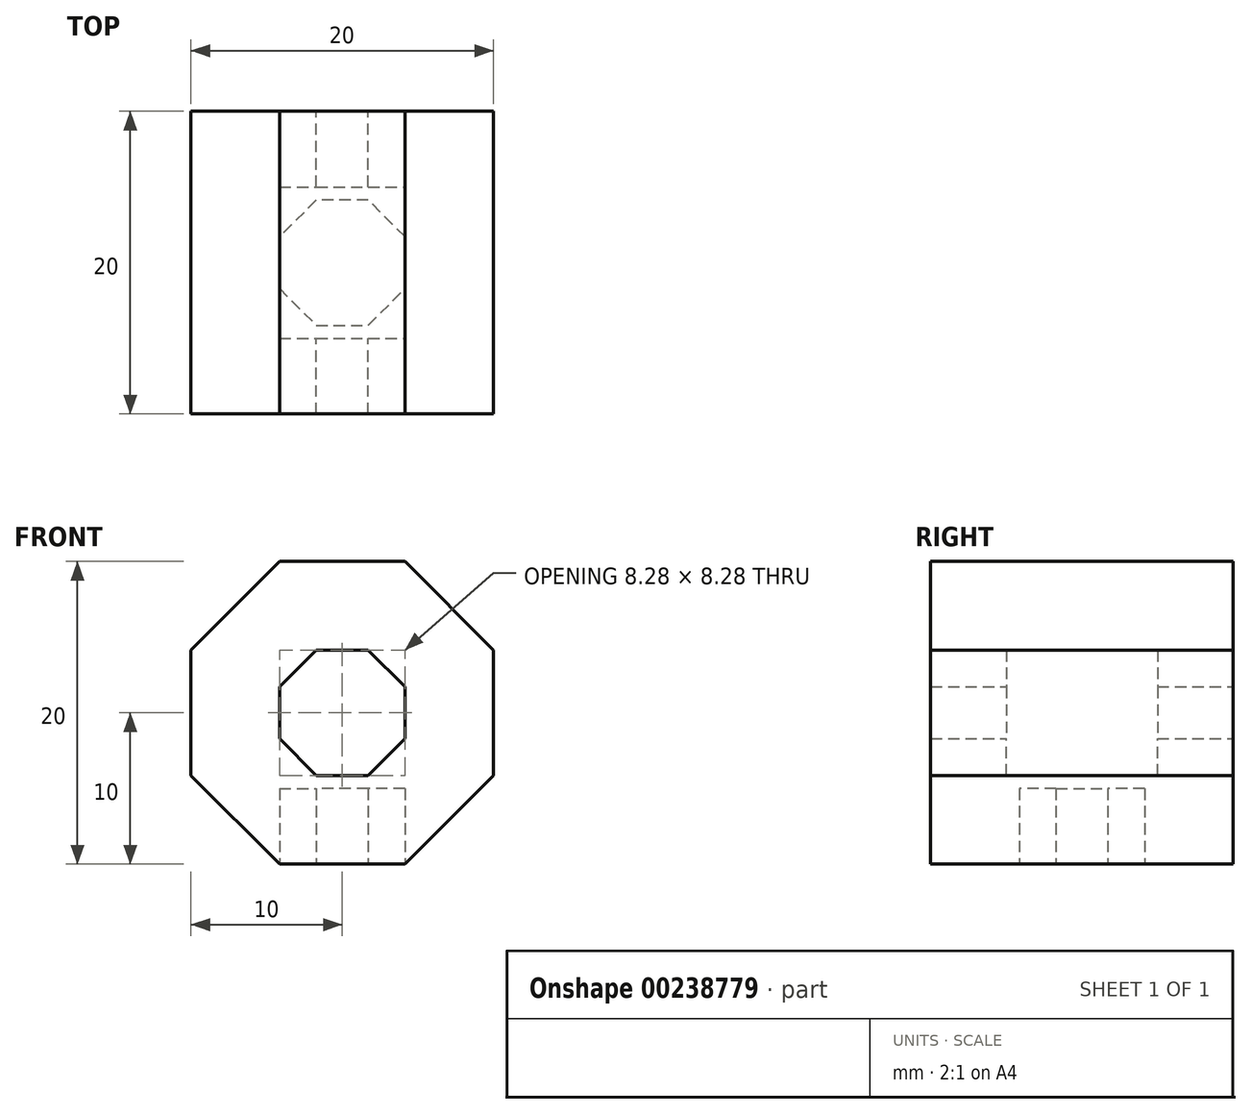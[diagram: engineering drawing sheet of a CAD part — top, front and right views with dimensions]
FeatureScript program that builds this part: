
annotation { "Feature Type Name" : "Feature", "Feature Type Description" : "" }
export const myFeature = defineFeature(function(context is Context, id is Id, definition is map)
    precondition{}
    {
        {
            var Q0;
            Q0=qCreatedBy(makeId("Front.planeOp"),FACE);
            var sketch = newSketch(context, id + "F0", { "sketchPlane" : qUnion([Q0])});
            skLineSegment(sketch, "E0.0", {"start": v(10, -4.14) * mm, "end": v(4.14, -10) * mm});
            skLineSegment(sketch, "E0.1", {"start": v(4.14, -10) * mm, "end": v(-4.14, -10) * mm});
            skLineSegment(sketch, "E0.2", {"start": v(-4.14, -10) * mm, "end": v(-10, -4.14) * mm});
            skLineSegment(sketch, "E0.3", {"start": v(-10, -4.14) * mm, "end": v(-10, 4.14) * mm});
            skLineSegment(sketch, "E0.4", {"start": v(-10, 4.14) * mm, "end": v(-4.14, 10) * mm});
            skLineSegment(sketch, "E0.5", {"start": v(-4.14, 10) * mm, "end": v(4.14, 10) * mm});
            skLineSegment(sketch, "E0.6", {"start": v(4.14, 10) * mm, "end": v(10, 4.14) * mm});
            skLineSegment(sketch, "E0.7", {"start": v(10, 4.14) * mm, "end": v(10, -4.14) * mm});
            skPoint(sketch, "E0.0.midPoint", {"position": v(7.07, -7.07) * mm});
            skLineSegment(sketch, "E1", {"start": v(-1.72, -4.14) * mm, "end": v(1.72, -4.14) * mm});
            skLineSegment(sketch, "E2.0", {"start": v(1.72, 4.14) * mm, "end": v(4.14, 1.72) * mm});
            skLineSegment(sketch, "E2.1", {"start": v(4.14, 1.72) * mm, "end": v(4.14, -1.72) * mm});
            skLineSegment(sketch, "E2.2", {"start": v(4.14, -1.72) * mm, "end": v(1.72, -4.14) * mm});
            skLineSegment(sketch, "E2.3", {"start": v(1.72, -4.14) * mm, "end": v(-1.72, -4.14) * mm});
            skLineSegment(sketch, "E2.4", {"start": v(-1.72, -4.14) * mm, "end": v(-4.14, -1.72) * mm});
            skLineSegment(sketch, "E2.5", {"start": v(-4.14, -1.72) * mm, "end": v(-4.14, 1.72) * mm});
            skLineSegment(sketch, "E2.6", {"start": v(-4.14, 1.72) * mm, "end": v(-1.72, 4.14) * mm});
            skLineSegment(sketch, "E2.7", {"start": v(-1.72, 4.14) * mm, "end": v(1.72, 4.14) * mm});
            skPoint(sketch, "E2.0.midPoint", {"position": v(2.93, 2.93) * mm});
            skPoint(sketch, "E3.orphan", {"position": v(0, -10) * mm});
            skPoint(sketch, "E4.orphan", {"position": v(0, 10) * mm});
            skPoint(sketch, "E5.orphan", {"position": v(-10, 0) * mm});
            skPoint(sketch, "E6.end.orphan", {"position": v(10, 0) * mm});
            skSolve(sketch);
        }
        {
            var Q0;
            Q0=makeQuery(id+"F0.imprint","IMPRINT",FACE,{"disambiguationData":[TD([[makeQuery(id+"F0.imprint","IMPRINT",EDGE,{"derivedFrom":sQuery(id+"F0.wireOp",EDGE,"E2.0")}),-1.0]])]});
            extrude(context, id + "F1", {"entities" : qUnion([Q0]), "depth" : 15 * mm});
        }
        {
            var Q0;
            Q0=makeQuery(id+"F0.imprint","IMPRINT",FACE,{"disambiguationData":[TD([[makeQuery(id+"F0.imprint","IMPRINT",EDGE,{"derivedFrom":sQuery(id+"F0.wireOp",EDGE,"E0.0")}),-1.0]])]});
            extrude(context, id + "F2", {"entities" : qUnion([Q0]), "operationType" : NewBodyOperationType.ADD, "depth" : 20 * mm});
        }
        {
            var Q0;
            Q0=makeQuery(id+"F0.imprint","IMPRINT",FACE,{"disambiguationData":[TD([[makeQuery(id+"F0.imprint","IMPRINT",EDGE,{"derivedFrom":sQuery(id+"F0.wireOp",EDGE,"E2.0")}),-1.0]])]});
            extrude(context, id + "F3", {"entities" : qUnion([Q0]), "operationType" : NewBodyOperationType.REMOVE, "depth" : 5 * mm});
        }
        {
            var Q0;
            Q0=makeQuery(id+"F2.opExtrude","SWEPT_FACE",FACE,{"disambiguationData":[OSD([sQuery(id+"F0.wireOp",EDGE,"E0.1")])]});
            var sketch = newSketch(context, id + "F4", { "sketchPlane" : qUnion([Q0])});
            skLineSegment(sketch, "E7.0", {"start": v(-4.14, 8.28) * mm, "end": v(-4.14, 11.72) * mm});
            skLineSegment(sketch, "E7.1", {"start": v(-4.14, 11.72) * mm, "end": v(-1.72, 14.14) * mm});
            skLineSegment(sketch, "E7.2", {"start": v(-1.72, 14.14) * mm, "end": v(1.72, 14.14) * mm});
            skLineSegment(sketch, "E7.3", {"start": v(1.72, 14.14) * mm, "end": v(4.14, 11.72) * mm});
            skLineSegment(sketch, "E7.4", {"start": v(4.14, 11.72) * mm, "end": v(4.14, 8.28) * mm});
            skLineSegment(sketch, "E7.5", {"start": v(4.14, 8.28) * mm, "end": v(1.72, 5.86) * mm});
            skLineSegment(sketch, "E7.6", {"start": v(1.72, 5.86) * mm, "end": v(-1.72, 5.86) * mm});
            skLineSegment(sketch, "E7.7", {"start": v(-1.72, 5.86) * mm, "end": v(-4.14, 8.28) * mm});
            skPoint(sketch, "E7.0.midPoint", {"position": v(-4.14, 10) * mm});
            skPoint(sketch, "E7.cCircle.center.orphan", {"position": v(0, 10) * mm});
            skSolve(sketch);
        }
        {
            var Q0;
            Q0=makeQuery(id+"F4.imprint","IMPRINT",FACE,{"disambiguationData":[TD([[makeQuery(id+"F4.imprint","IMPRINT",EDGE,{"derivedFrom":sQuery(id+"F4.wireOp",EDGE,"E7.0")}),1.0]])]});
            extrude(context, id + "F5", {"entities" : qUnion([Q0]), "operationType" : NewBodyOperationType.REMOVE, "oppositeDirection" : true, "depth" : 5 * mm});
        }
        {
            var Q0;
            Q0=qCreatedBy(makeId("Right.planeOp"),FACE);
            var sketch = newSketch(context, id + "F6", { "sketchPlane" : qUnion([Q0])});
            skLineSegment(sketch, "E8", {"start": v(-44.65, 0) * mm, "end": v(29.32, 0) * mm});
            skSolve(sketch);
        }
    });
